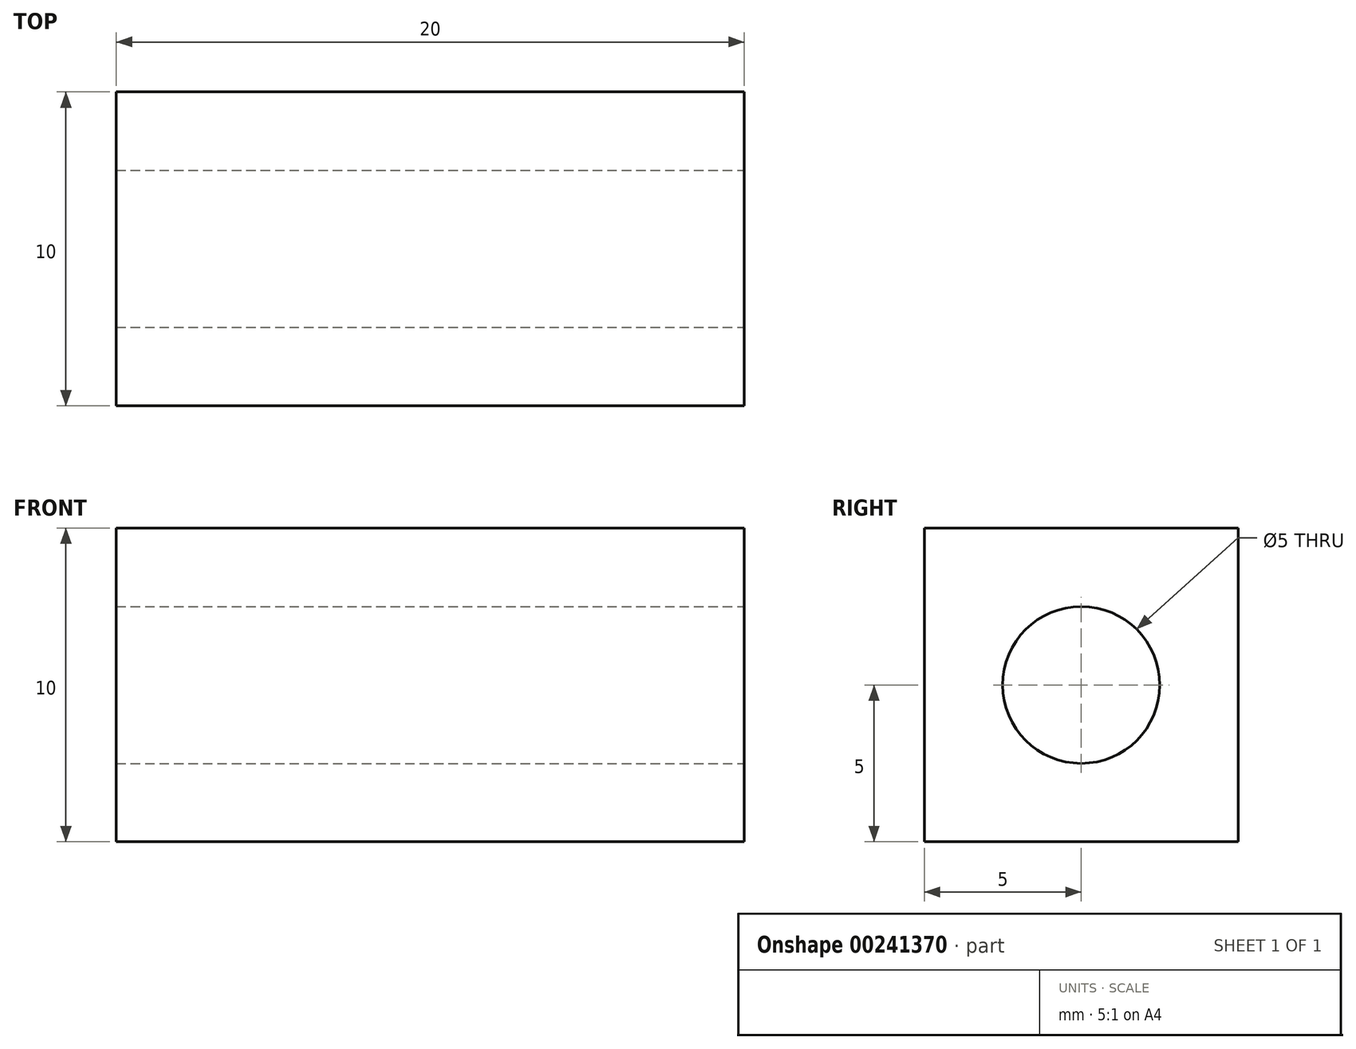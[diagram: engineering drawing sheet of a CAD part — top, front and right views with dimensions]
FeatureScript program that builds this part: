
annotation { "Feature Type Name" : "Feature", "Feature Type Description" : "" }
export const myFeature = defineFeature(function(context is Context, id is Id, definition is map)
    precondition{}
    {
        {
            var Q0;
            Q0=qCreatedBy(makeId("Front.planeOp"),FACE);
            var sketch = newSketch(context, id + "F0", { "sketchPlane" : qUnion([Q0])});
            skLineSegment(sketch, "E0.bottom", {"start": v(-10, 5) * mm, "end": v(10, 5) * mm});
            skLineSegment(sketch, "E0.top", {"start": v(-10, -5) * mm, "end": v(10, -5) * mm});
            skLineSegment(sketch, "E0.left", {"start": v(-10, 5) * mm, "end": v(-10, -5) * mm});
            skLineSegment(sketch, "E0.right", {"start": v(10, 5) * mm, "end": v(10, -5) * mm});
            skPoint(sketch, "E0.middle", {"position": v(0, 0) * mm});
            skSolve(sketch);
        }
        {
            var Q0;
            Q0=qSketchRegion(id+"F0",true);
            extrude(context, id + "F1", {"entities" : qUnion([Q0]), "depth" : 10 * mm});
        }
        {
            var Q0;
            Q0=makeQuery(id+"F1.opExtrude","SWEPT_FACE",FACE,{"disambiguationData":[OSD([sQuery(id+"F0.wireOp",EDGE,"E0.right")])]});
            var sketch = newSketch(context, id + "F2", { "sketchPlane" : qUnion([Q0])});
            skCircle(sketch, "E1", {"center": v(-5, 0) * mm, "radius": 2.5 * mm});
            skPoint(sketch, "E1.centerSnap0", {"position": v(-10, 0) * mm});
            skPoint(sketch, "E1.centerSnap1", {"position": v(-5, 5) * mm});
            skSolve(sketch);
        }
        {
            var Q0;
            Q0=qSketchRegion(id+"F2",true);
            extrude(context, id + "F3", {"entities" : qUnion([Q0]), "operationType" : NewBodyOperationType.REMOVE, "endBound" : BoundingType.THROUGH_ALL, "oppositeDirection" : true, "depth" : 25 * mm});
        }
    });
